FCSTD DOCUMENT  (FreeCAD 0.18.4R)
Label: our_room
License: All rights reserved
LicenseURL: http://en.wikipedia.org/wiki/All_rights_reserved
objects: Part::Part2DObjectPython×3, App::Part×1, Part::FeaturePython×1
note: 4 computed .brp shape members not serialized (recipe doc carries the construction recipe); baked Part::Feature solids carry a one-line shape summary decoded from their .brp

FEATURE [App::Part] Part
  Origin = -> Origin
FEATURE [Part::Part2DObjectPython] Line  # Draft 2D object (typed FeaturePython)
  ChamferSize = 0
  Closed = true
  End = (0,0,0)
  FilletRadius = 0
  Length = 4620
  MakeFace = false
  Points = (2) [(4620,1.41447e-13,0),(0,0,0)]
  Start = (4620,2.829e-13,0)
  Subdivisions = 0
FEATURE [Part::Part2DObjectPython] Line001  # Draft 2D object (typed FeaturePython)
  ChamferSize = 0
  Closed = true
  End = (4620,1155,0)
  FilletRadius = 0
  Length = 1155
  MakeFace = false
  Placement = pos=(4620,2.829e-13,0) rot=(0,0,1;0rad)
  Points = (2) [(0,0,0),(0,1155,0)]
  Start = (4620,2.829e-13,0)
  Subdivisions = 0
FEATURE [Part::FeaturePython] Point  # WARN: FeaturePython — macro-defined, semantics opaque (R4)
  X = 4620
  Y = 1155
  Z = 0
FEATURE [Part::Part2DObjectPython] Line003  # Draft 2D object (typed FeaturePython)
  ChamferSize = 0
  Closed = false
  End = (4710,1155,0)
  FilletRadius = 0
  Length = 4149
  MakeFace = true
  Points = (2) [(4620,1155,0),(4710,1155,0)]
  Start = (4620,1155,0)
  Subdivisions = 0
  expr: End.x = 462 + 9
